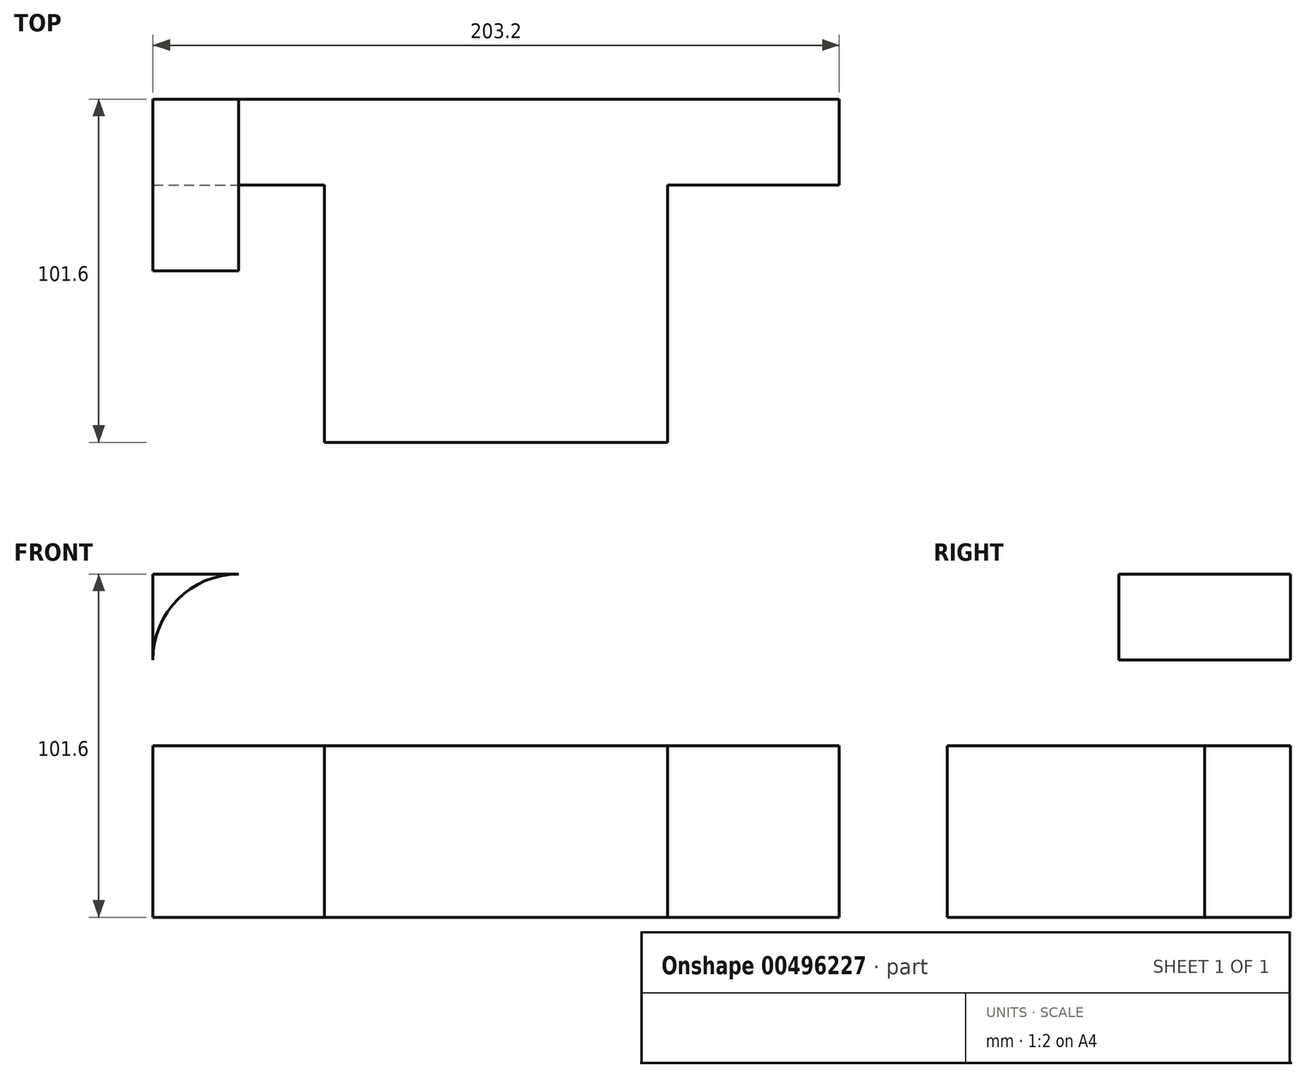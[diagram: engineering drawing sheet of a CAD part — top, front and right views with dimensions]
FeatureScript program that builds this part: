
annotation { "Feature Type Name" : "Feature", "Feature Type Description" : "" }
export const myFeature = defineFeature(function(context is Context, id is Id, definition is map)
    precondition{}
    {
        {
            var Q0;
            Q0=qCreatedBy(makeId("Top.planeOp"),FACE);
            var sketch = newSketch(context, id + "F0", { "sketchPlane" : qUnion([Q0])});
            skLineSegment(sketch, "E0.bottom", {"start": v(-67.36, 22.6) * mm, "end": v(135.84, 22.6) * mm});
            skLineSegment(sketch, "E0.top", {"start": v(-67.36, -28.2) * mm, "end": v(135.84, -28.2) * mm});
            skLineSegment(sketch, "E0.left", {"start": v(-67.36, 22.6) * mm, "end": v(-67.36, -28.2) * mm});
            skLineSegment(sketch, "E0.right", {"start": v(135.84, 22.6) * mm, "end": v(135.84, -28.2) * mm});
            skSolve(sketch);
        }
        {
            var Q0;
            Q0=makeQuery(id+"F0.imprint","IMPRINT",FACE,{"disambiguationData":[TD([[makeQuery(id+"F0.imprint","IMPRINT",EDGE,{"derivedFrom":sQuery(id+"F0.wireOp",EDGE,"E0.bottom")}),-1.0]])]});
            extrude(context, id + "F1", {"entities" : qUnion([Q0]), "depth" : 101.6 * mm});
        }
        {
            var Q0;
            Q0=makeQuery(id+"F1.opExtrude","SWEPT_FACE",FACE,{"disambiguationData":[OSD([sQuery(id+"F0.wireOp",EDGE,"E0.right")])]});
            var sketch = newSketch(context, id + "F2", { "sketchPlane" : qUnion([Q0])});
            skLineSegment(sketch, "E1.bottom", {"start": v(-28.2, 0) * mm, "end": v(-2.8, 0) * mm});
            skLineSegment(sketch, "E1.top", {"start": v(-28.2, 50.8) * mm, "end": v(-2.8, 50.8) * mm});
            skLineSegment(sketch, "E1.left", {"start": v(-28.2, 0) * mm, "end": v(-28.2, 50.8) * mm});
            skLineSegment(sketch, "E1.right", {"start": v(-2.8, 0) * mm, "end": v(-2.8, 50.8) * mm});
            skSolve(sketch);
        }
        {
            var Q0;
            Q0=makeQuery(id+"F2.imprint","IMPRINT",FACE,{"disambiguationData":[TD([[makeQuery(id+"F2.imprint","IMPRINT",EDGE,{"derivedFrom":sQuery(id+"F2.wireOp",EDGE,"E1.bottom")}),-1.0]])]});
            extrude(context, id + "F3", {"entities" : qUnion([Q0]), "operationType" : NewBodyOperationType.REMOVE, "endBound" : BoundingType.UP_TO_NEXT, "oppositeDirection" : true, "depth" : 25.4 * mm});
        }
        {
            var Q0;
            Q0=makeQuery(id+"F3.boolean.opBoolean","COPY",FACE,{"derivedFrom":makeQuery(id+"F3.opExtrude","SWEPT_FACE",FACE,{"disambiguationData":[OSD([sQuery(id+"F2.wireOp",EDGE,"E1.right")])]})});
            var sketch = newSketch(context, id + "F4", { "sketchPlane" : qUnion([Q0])});
            skLineSegment(sketch, "E2.bottom", {"start": v(-16.56, 0) * mm, "end": v(85.04, 0) * mm});
            skLineSegment(sketch, "E2.top", {"start": v(-16.56, 50.8) * mm, "end": v(85.04, 50.8) * mm});
            skLineSegment(sketch, "E2.left", {"start": v(-16.56, 0) * mm, "end": v(-16.56, 50.8) * mm});
            skLineSegment(sketch, "E2.right", {"start": v(85.04, 0) * mm, "end": v(85.04, 50.8) * mm});
            skSolve(sketch);
        }
        {
            var Q0;
            Q0=makeQuery(id+"F4.imprint","IMPRINT",FACE,{"disambiguationData":[TD([[makeQuery(id+"F4.imprint","IMPRINT",EDGE,{"derivedFrom":sQuery(id+"F4.wireOp",EDGE,"E2.bottom")}),1.0]])]});
            extrude(context, id + "F5", {"entities" : qUnion([Q0]), "operationType" : NewBodyOperationType.ADD, "depth" : 76.2 * mm});
        }
        {
            var Q0;
            Q0=makeQuery(id+"F1.opExtrude","SWEPT_FACE",FACE,{"disambiguationData":[OSD([sQuery(id+"F0.wireOp",EDGE,"E0.top")])]});
            var sketch = newSketch(context, id + "F6", { "sketchPlane" : qUnion([Q0])});
            skCircle(sketch, "E3", {"center": v(-41.96, 76.2) * mm, "radius": 12.7 * mm});
            skCircle(sketch, "E4", {"center": v(110.44, 76.2) * mm, "radius": 12.7 * mm});
            skArc(sketch, "E5", {"start": v(-67.36, 76.2) * mm, "mid": v(-59.92, 94.16) * mm, "end": v(-41.96, 101.6) * mm});
            skArc(sketch, "E6", {"start": v(135.84, 76.2) * mm, "mid": v(128.4, 94.16) * mm, "end": v(110.44, 101.6) * mm});
            skSolve(sketch);
        }
        {
            var Q0;
            Q0=makeQuery(id+"F6.imprint","IMPRINT",FACE,{"disambiguationData":[TD([[makeQuery(id+"F6.imprint","IMPRINT",EDGE,{"derivedFrom":sQuery(id+"F6.wireOp",EDGE,"E3")}),1.0]])]});
            var Q1;
            Q1=makeQuery(id+"F6.imprint","IMPRINT",FACE,{"disambiguationData":[TD([[makeQuery(id+"F6.imprint","IMPRINT",EDGE,{"derivedFrom":sQuery(id+"F6.wireOp",EDGE,"E4")}),1.0]])]});
            var Q2;
            {var subQ0=sQuery(id+"F6.wireOp",EDGE,"E5");Q2=makeQuery(id+"F6.imprint","IMPRINT",FACE,{"disambiguationData":[TD([[makeQuery(id+"F6.imprint","IMPRINT",EDGE,{"derivedFrom":subQ0}),1.0]])]});}
            var Q3;
            {var subQ0=sQuery(id+"F6.wireOp",EDGE,"E6");Q3=makeQuery(id+"F6.imprint","IMPRINT",FACE,{"disambiguationData":[TD([[makeQuery(id+"F6.imprint","IMPRINT",EDGE,{"derivedFrom":subQ0}),-1.0]])]});}
            extrude(context, id + "F7", {"entities" : qUnion([Q0, Q1, Q2, Q3]), "operationType" : NewBodyOperationType.REMOVE, "endBound" : BoundingType.UP_TO_NEXT, "oppositeDirection" : true, "depth" : 25.4 * mm});
        }
    });
